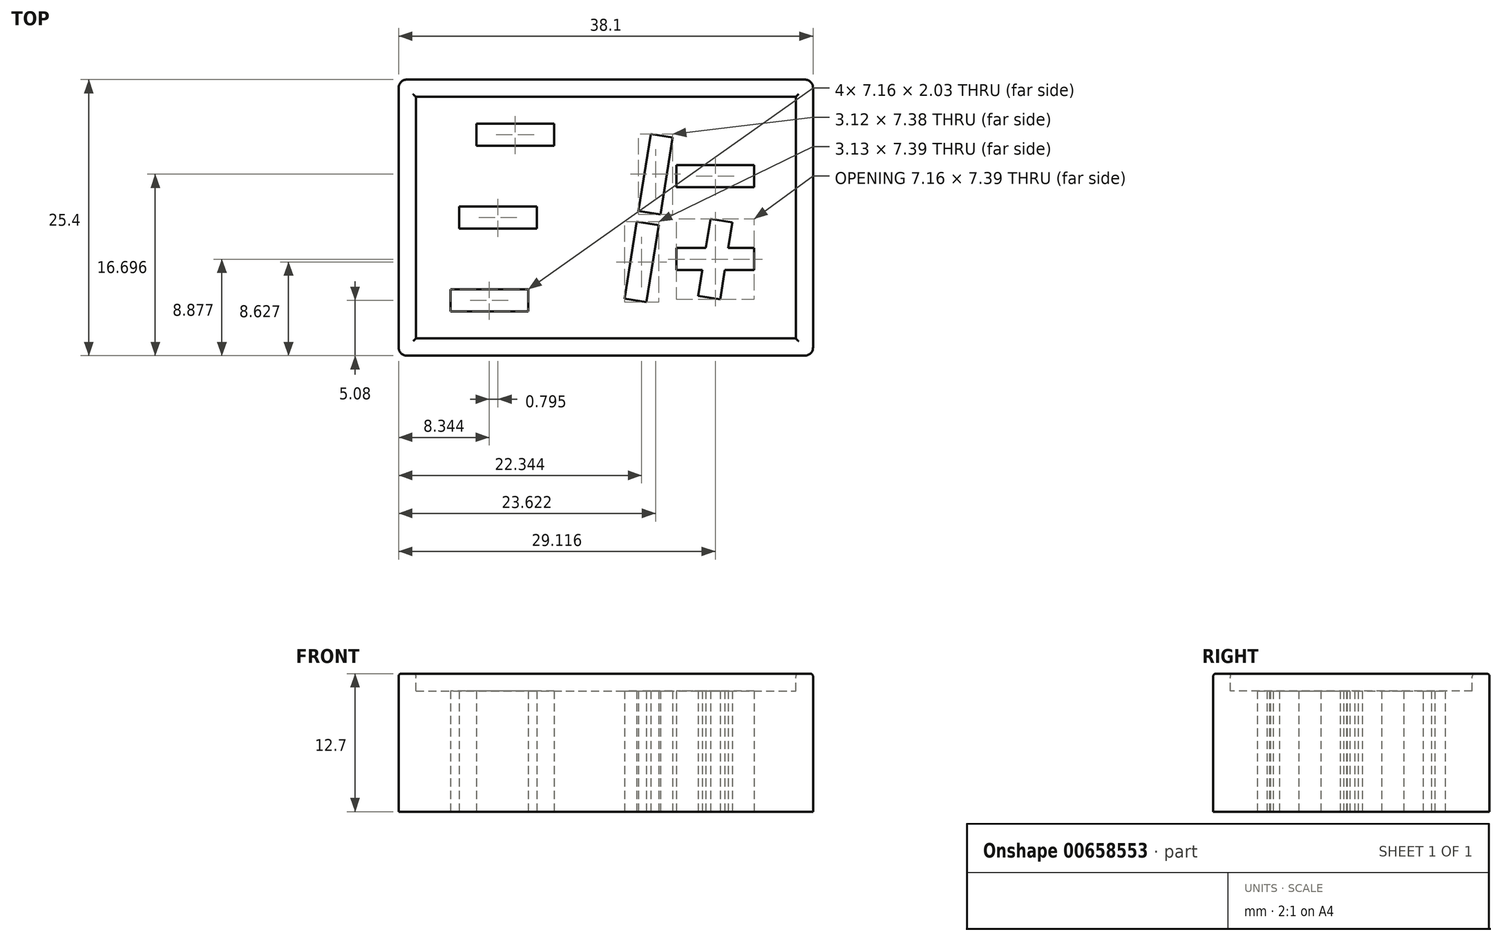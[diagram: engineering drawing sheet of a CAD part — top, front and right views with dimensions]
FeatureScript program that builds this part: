
annotation { "Feature Type Name" : "Feature", "Feature Type Description" : "" }
export const myFeature = defineFeature(function(context is Context, id is Id, definition is map)
    precondition{}
    {
        {
            var Q0;
            Q0=qCreatedBy(makeId("Top.planeOp"),FACE);
            var sketch = newSketch(context, id + "F0", { "sketchPlane" : qUnion([Q0])});
            skLineSegment(sketch, "E0.bottom", {"start": v(-19.05, 12.7) * mm, "end": v(19.05, 12.7) * mm});
            skLineSegment(sketch, "E0.top", {"start": v(-19.05, -12.7) * mm, "end": v(19.05, -12.7) * mm});
            skLineSegment(sketch, "E0.left", {"start": v(-19.05, 12.7) * mm, "end": v(-19.05, -12.7) * mm});
            skLineSegment(sketch, "E0.right", {"start": v(19.05, 12.7) * mm, "end": v(19.05, -12.7) * mm});
            skSolve(sketch);
        }
        {
            var Q0;
            Q0=qSketchRegion(id+"F0",true);
            extrude(context, id + "F1", {"entities" : qUnion([Q0]), "depth" : 12.7 * mm, "offsetDistance" : 25.4 * mm});
        }
        {
            var Q0;
            Q0=makeQuery(id+"F1.opExtrude","CAP_FACE",FACE,{"disambiguationData":[OSD([sQuery(id+"F0.wireOp",EDGE,"E0.bottom"),sQuery(id+"F0.wireOp",EDGE,"E0.top"),sQuery(id+"F0.wireOp",EDGE,"E0.left"),sQuery(id+"F0.wireOp",EDGE,"E0.right")])],"isStart":false});
            var sketch = newSketch(context, id + "F2", { "sketchPlane" : qUnion([Q0])});
            skLineSegment(sketch, "E1.bottom", {"start": v(-17.46, 11.11) * mm, "end": v(17.46, 11.11) * mm});
            skLineSegment(sketch, "E1.top", {"start": v(-17.46, -11.11) * mm, "end": v(17.46, -11.11) * mm});
            skLineSegment(sketch, "E1.left", {"start": v(-17.46, 11.11) * mm, "end": v(-17.46, -11.11) * mm});
            skLineSegment(sketch, "E1.right", {"start": v(17.46, 11.11) * mm, "end": v(17.46, -11.11) * mm});
            skSolve(sketch);
        }
        {
            var Q0;
            Q0=qSketchRegion(id+"F2",true);
            extrude(context, id + "F3", {"entities" : qUnion([Q0]), "operationType" : NewBodyOperationType.REMOVE, "oppositeDirection" : true, "depth" : 1.59 * mm, "offsetDistance" : 25.4 * mm});
        }
        {
            var Q0;
            Q0=makeQuery(id+"F1.opExtrude","SWEPT_EDGE",EDGE,{"disambiguationData":[OSD([sQuery(id+"F0.wireOp",EDGE,"E0.top"),sQuery(id+"F0.wireOp",EDGE,"E0.left")])]});
            var Q1;
            Q1=makeQuery(id+"F1.opExtrude","SWEPT_EDGE",EDGE,{"disambiguationData":[OSD([sQuery(id+"F0.wireOp",EDGE,"E0.bottom"),sQuery(id+"F0.wireOp",EDGE,"E0.left")])]});
            var Q2;
            Q2=makeQuery(id+"F1.opExtrude","SWEPT_EDGE",EDGE,{"disambiguationData":[OSD([sQuery(id+"F0.wireOp",EDGE,"E0.bottom"),sQuery(id+"F0.wireOp",EDGE,"E0.right")])]});
            var Q3;
            Q3=makeQuery(id+"F1.opExtrude","SWEPT_EDGE",EDGE,{"disambiguationData":[OSD([sQuery(id+"F0.wireOp",EDGE,"E0.top"),sQuery(id+"F0.wireOp",EDGE,"E0.right")])]});
            fillet(context, id + "F4", {"entities" : qUnion([Q0, Q1, Q2, Q3]), "radius" : 0.76 * mm, "tangentPropagation" : true, "allowEdgeOverflow" : false});
        }
        {
            var Q0;
            Q0=makeQuery(id+"F1.opExtrude","CAP_FACE",FACE,{"disambiguationData":[OSD([sQuery(id+"F0.wireOp",EDGE,"E0.bottom"),sQuery(id+"F0.wireOp",EDGE,"E0.top"),sQuery(id+"F0.wireOp",EDGE,"E0.left"),sQuery(id+"F0.wireOp",EDGE,"E0.right")])],"isStart":false});
            fillet(context, id + "F5", {"entities" : qUnion([Q0]), "radius" : 0.25 * mm, "tangentPropagation" : true, "allowEdgeOverflow" : false});
        }
        {
            var Q0;
            Q0=qCreatedBy(makeId("Top.planeOp"),FACE);
            var sketch = newSketch(context, id + "F6", { "sketchPlane" : qUnion([Q0])});
            skLineSegment(sketch, "E2.bottom", {"start": v(-14.29, -6.6) * mm, "end": v(-7.12, -6.6) * mm});
            skLineSegment(sketch, "E2.top", {"start": v(-14.29, -8.64) * mm, "end": v(-7.12, -8.64) * mm});
            skLineSegment(sketch, "E2.left", {"start": v(-14.29, -6.6) * mm, "end": v(-14.29, -8.64) * mm});
            skLineSegment(sketch, "E2.right", {"start": v(-7.12, -6.6) * mm, "end": v(-7.12, -8.64) * mm});
            skLineSegment(sketch, "E3.bottom", {"start": v(-13.5, 1.02) * mm, "end": v(-6.33, 1.02) * mm});
            skLineSegment(sketch, "E3.top", {"start": v(-13.5, -1.02) * mm, "end": v(-6.33, -1.02) * mm});
            skLineSegment(sketch, "E3.left", {"start": v(-13.5, 1.02) * mm, "end": v(-13.5, -1.02) * mm});
            skLineSegment(sketch, "E3.right", {"start": v(-6.33, 1.02) * mm, "end": v(-6.33, -1.02) * mm});
            skLineSegment(sketch, "E4.bottom", {"start": v(-11.9, 8.64) * mm, "end": v(-4.74, 8.64) * mm});
            skLineSegment(sketch, "E4.top", {"start": v(-11.9, 6.6) * mm, "end": v(-4.74, 6.6) * mm});
            skLineSegment(sketch, "E4.left", {"start": v(-11.9, 8.64) * mm, "end": v(-11.9, 6.6) * mm});
            skLineSegment(sketch, "E4.right", {"start": v(-4.74, 8.64) * mm, "end": v(-4.74, 6.6) * mm});
            skLineSegment(sketch, "E5.bottom", {"start": v(6.48, 4.83) * mm, "end": v(13.65, 4.83) * mm});
            skLineSegment(sketch, "E5.top", {"start": v(6.48, 2.8) * mm, "end": v(13.65, 2.8) * mm});
            skLineSegment(sketch, "E5.left", {"start": v(6.48, 4.83) * mm, "end": v(6.48, 2.8) * mm});
            skLineSegment(sketch, "E5.right", {"start": v(13.65, 4.83) * mm, "end": v(13.65, 2.8) * mm});
            skLineSegment(sketch, "E6.bottom", {"start": v(6.48, -2.8) * mm, "end": v(13.65, -2.8) * mm});
            skLineSegment(sketch, "E6.top", {"start": v(6.48, -4.83) * mm, "end": v(13.65, -4.83) * mm});
            skLineSegment(sketch, "E6.left", {"start": v(6.48, -2.8) * mm, "end": v(6.48, -4.83) * mm});
            skLineSegment(sketch, "E6.right", {"start": v(13.65, -2.8) * mm, "end": v(13.65, -4.83) * mm});
            skLineSegment(sketch, "E7", {"start": v(6.13, 7.37) * mm, "end": v(5.02, 0.3) * mm});
            skLineSegment(sketch, "E8", {"start": v(5.02, 0.3) * mm, "end": v(3, 0.63) * mm});
            skLineSegment(sketch, "E9", {"start": v(3, 0.63) * mm, "end": v(4.13, 7.68) * mm});
            skLineSegment(sketch, "E10", {"start": v(4.13, 7.68) * mm, "end": v(6.13, 7.37) * mm});
            skLineSegment(sketch, "E11", {"start": v(11.63, -0.44) * mm, "end": v(10.5, -7.52) * mm});
            skLineSegment(sketch, "E12", {"start": v(11.63, -0.44) * mm, "end": v(9.62, -0.13) * mm});
            skLineSegment(sketch, "E13", {"start": v(9.62, -0.13) * mm, "end": v(8.5, -7.18) * mm});
            skLineSegment(sketch, "E14", {"start": v(8.5, -7.18) * mm, "end": v(10.5, -7.52) * mm});
            skLineSegment(sketch, "E15", {"start": v(4.86, -0.7) * mm, "end": v(3.74, -7.77) * mm});
            skLineSegment(sketch, "E16", {"start": v(4.86, -0.7) * mm, "end": v(2.85, -0.38) * mm});
            skLineSegment(sketch, "E17", {"start": v(3.74, -7.77) * mm, "end": v(1.73, -7.45) * mm});
            skLineSegment(sketch, "E18", {"start": v(1.73, -7.45) * mm, "end": v(2.85, -0.38) * mm});
            skSolve(sketch);
        }
        {
            var Q0;
            Q0=qSketchRegion(id+"F6",true);
            extrude(context, id + "F7", {"entities" : qUnion([Q0]), "operationType" : NewBodyOperationType.REMOVE, "depth" : 25.4 * mm, "offsetDistance" : 25.4 * mm});
        }
    });
